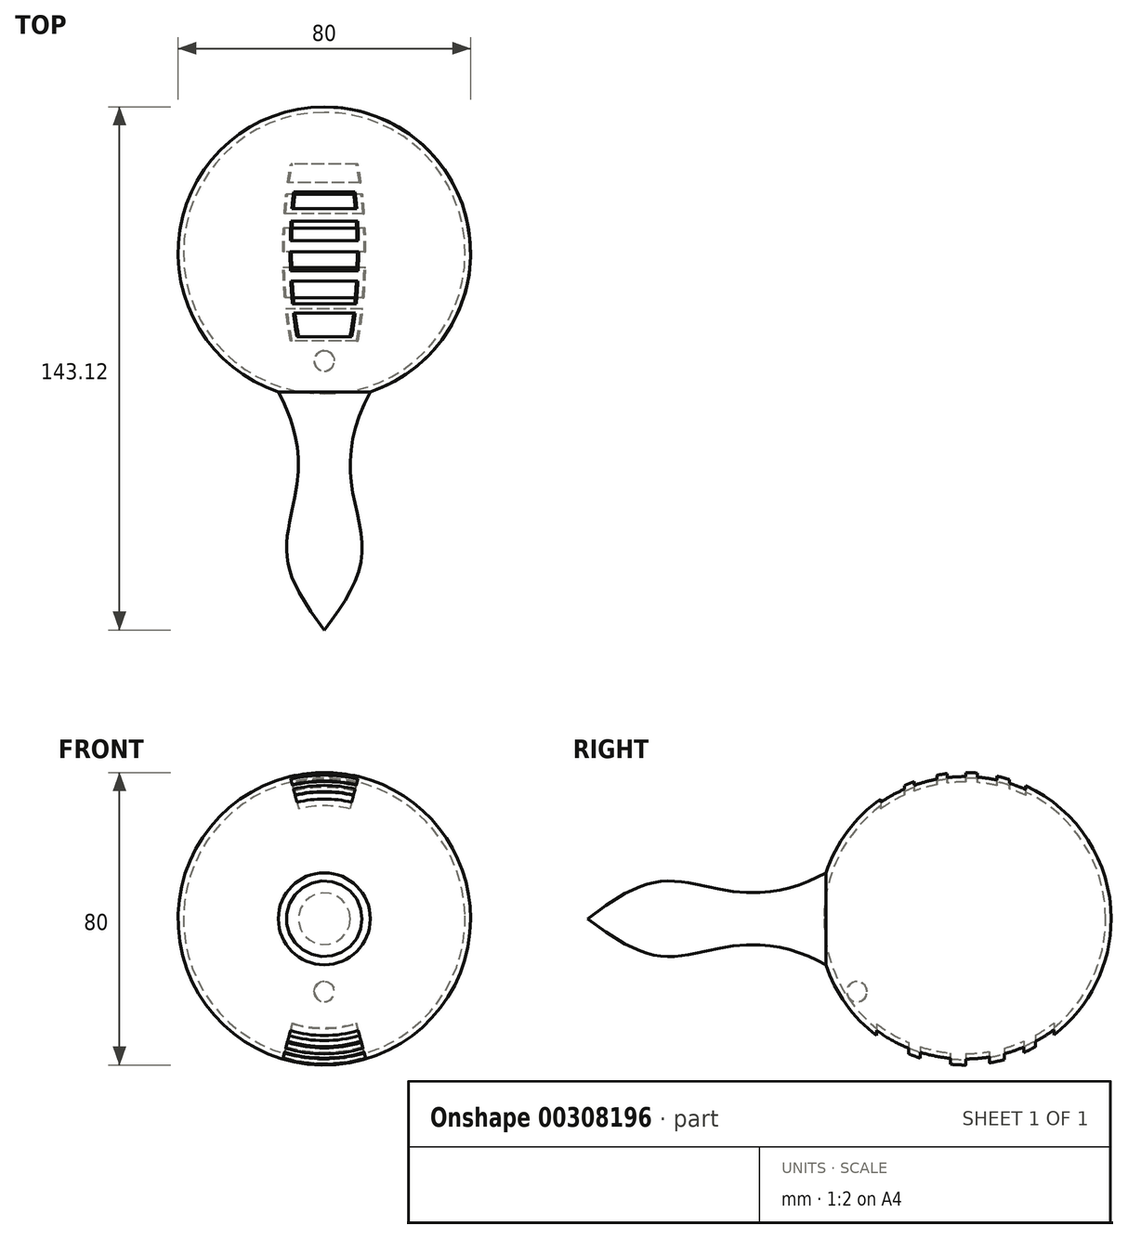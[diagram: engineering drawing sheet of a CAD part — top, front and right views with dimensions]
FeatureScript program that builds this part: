
annotation { "Feature Type Name" : "Feature", "Feature Type Description" : "" }
export const myFeature = defineFeature(function(context is Context, id is Id, definition is map)
    precondition{}
    {
        {
            var Q0;
            Q0=qCreatedBy(makeId("Top.planeOp"),FACE);
            var sketch = newSketch(context, id + "F0", { "sketchPlane" : qUnion([Q0])});
            skArc(sketch, "E0", {"start": v(0, -3.6) * mm, "mid": v(40, 36.4) * mm, "end": v(0, 76.4) * mm});
            skArc(sketch, "E1", {"start": v(0, -2.1) * mm, "mid": v(38.5, 36.4) * mm, "end": v(0, 74.9) * mm});
            skLineSegment(sketch, "E2", {"start": v(0, 76.4) * mm, "end": v(0, -3.6) * mm, "construction": true});
            skLineSegment(sketch, "E3", {"start": v(0, 76.4) * mm, "end": v(0, 74.9) * mm});
            skLineSegment(sketch, "E4", {"start": v(0, -3.6) * mm, "end": v(0, -2.1) * mm});
            skLineSegment(sketch, "E5", {"start": v(12.57, -1.57) * mm, "end": v(12.57, -66.72) * mm, "construction": true});
            skLineSegment(sketch, "E6", {"start": v(12.57, -66.72) * mm, "end": v(0, -66.72) * mm, "construction": true});
            skLineSegment(sketch, "E7", {"start": v(0, -66.72) * mm, "end": v(0, -3.6) * mm, "construction": true});
            skFitSpline(sketch, "E8", {"points": [v(12.57, -1.57) * mm, v(7.43, -26.75) * mm, v(10.25, -46.34) * mm, v(0, -66.72) * mm], "startDerivative": vector(-42.55, -78.05) * mm, "endDerivative": vector(-48.97, -63.58) * mm});
            skLineSegment(sketch, "E9", {"start": v(0, -3.6) * mm, "end": v(0, -66.72) * mm});
            skSolve(sketch);
        }
        {
            var Q0;
            {var subQ2=sQuery(id+"F0.wireOp",EDGE,"E8");Q0=makeQuery(id+"F0.imprint","IMPRINT",FACE,{"disambiguationData":[TD([[makeQuery(id+"F0.imprint","IMPRINT",EDGE,{"derivedFrom":subQ2}),-1.0]])]});}
            var Q1;
            Q1=makeQuery(id+"F0.imprint","IMPRINT",FACE,{"disambiguationData":[TD([[makeQuery(id+"F0.imprint","IMPRINT",EDGE,{"derivedFrom":sQuery(id+"F0.wireOp",EDGE,"E1")}),-1.0]])]});
            var Q2;
            Q2=sQuery(id+"F0.wireOp",EDGE,"E9");
            revolve(context, id + "F1", {"entities" : qUnion([Q0, Q1]), "axis" : qUnion([Q2]), "revolveType" : RevolveType.FULL});
        }
        {
            var Q0;
            Q0=qCreatedBy(makeId("Right.planeOp"),FACE);
            var sketch = newSketch(context, id + "F2", { "sketchPlane" : qUnion([Q0])});
            skLineSegment(sketch, "E10.bottom", {"start": v(13.45, 41.36) * mm, "end": v(19.96, 41.36) * mm});
            skLineSegment(sketch, "E10.top", {"start": v(13.45, 6.23) * mm, "end": v(19.96, 6.23) * mm});
            skLineSegment(sketch, "E10.left", {"start": v(13.45, 41.36) * mm, "end": v(13.45, 6.23) * mm});
            skLineSegment(sketch, "E10.right", {"start": v(19.96, 41.36) * mm, "end": v(19.96, 6.23) * mm});
            skLineSegment(sketch, "E11.bottom", {"start": v(28.74, 41.36) * mm, "end": v(22.51, 41.36) * mm});
            skLineSegment(sketch, "E11.top", {"start": v(28.74, 5.38) * mm, "end": v(22.51, 5.38) * mm});
            skLineSegment(sketch, "E11.left", {"start": v(28.74, 41.36) * mm, "end": v(28.74, 5.38) * mm});
            skLineSegment(sketch, "E11.right", {"start": v(22.51, 41.36) * mm, "end": v(22.51, 5.38) * mm});
            skLineSegment(sketch, "E12.bottom", {"start": v(31.58, 41.64) * mm, "end": v(36.67, 41.64) * mm});
            skLineSegment(sketch, "E12.top", {"start": v(31.58, 3.97) * mm, "end": v(36.67, 3.97) * mm});
            skLineSegment(sketch, "E12.left", {"start": v(31.58, 41.64) * mm, "end": v(31.58, 3.97) * mm});
            skLineSegment(sketch, "E12.right", {"start": v(36.67, 41.64) * mm, "end": v(36.67, 3.97) * mm});
            skLineSegment(sketch, "E13.bottom", {"start": v(39.8, 41.64) * mm, "end": v(45.17, 41.64) * mm});
            skLineSegment(sketch, "E13.top", {"start": v(39.8, 4.25) * mm, "end": v(45.17, 4.25) * mm});
            skLineSegment(sketch, "E13.left", {"start": v(39.8, 41.64) * mm, "end": v(39.8, 4.25) * mm});
            skLineSegment(sketch, "E13.right", {"start": v(45.17, 41.64) * mm, "end": v(45.17, 4.25) * mm});
            skLineSegment(sketch, "E14.bottom", {"start": v(48.57, 41.64) * mm, "end": v(53.1, 41.64) * mm});
            skLineSegment(sketch, "E14.top", {"start": v(48.57, 3.97) * mm, "end": v(53.1, 3.97) * mm});
            skLineSegment(sketch, "E14.left", {"start": v(48.57, 41.64) * mm, "end": v(48.57, 3.97) * mm});
            skLineSegment(sketch, "E14.right", {"start": v(53.1, 41.64) * mm, "end": v(53.1, 3.97) * mm});
            skLineSegment(sketch, "E15.bottom", {"start": v(12.31, -15.01) * mm, "end": v(21.1, -15.01) * mm});
            skLineSegment(sketch, "E15.top", {"start": v(12.31, -49) * mm, "end": v(21.1, -49) * mm});
            skLineSegment(sketch, "E15.left", {"start": v(12.31, -15.01) * mm, "end": v(12.31, -49) * mm});
            skLineSegment(sketch, "E15.right", {"start": v(21.1, -15.01) * mm, "end": v(21.1, -49) * mm});
            skLineSegment(sketch, "E16.bottom", {"start": v(24.21, -15.3) * mm, "end": v(32.43, -15.3) * mm});
            skLineSegment(sketch, "E16.top", {"start": v(24.21, -48.44) * mm, "end": v(32.43, -48.44) * mm});
            skLineSegment(sketch, "E16.left", {"start": v(24.21, -15.3) * mm, "end": v(24.21, -48.44) * mm});
            skLineSegment(sketch, "E16.right", {"start": v(32.43, -15.3) * mm, "end": v(32.43, -48.44) * mm});
            skLineSegment(sketch, "E17.bottom", {"start": v(36.67, -15.58) * mm, "end": v(43.19, -15.58) * mm});
            skLineSegment(sketch, "E17.top", {"start": v(36.67, -49) * mm, "end": v(43.19, -49) * mm});
            skLineSegment(sketch, "E17.left", {"start": v(36.67, -15.58) * mm, "end": v(36.67, -49) * mm});
            skLineSegment(sketch, "E17.right", {"start": v(43.19, -15.58) * mm, "end": v(43.19, -49) * mm});
            skLineSegment(sketch, "E18.bottom", {"start": v(47.16, -15.01) * mm, "end": v(52.54, -15.01) * mm});
            skLineSegment(sketch, "E18.top", {"start": v(47.16, -49.29) * mm, "end": v(52.54, -49.29) * mm});
            skLineSegment(sketch, "E18.left", {"start": v(47.16, -15.01) * mm, "end": v(47.16, -49.29) * mm});
            skLineSegment(sketch, "E18.right", {"start": v(52.54, -15.01) * mm, "end": v(52.54, -49.29) * mm});
            skLineSegment(sketch, "E19.bottom", {"start": v(55.65, -15.58) * mm, "end": v(60.75, -15.58) * mm});
            skLineSegment(sketch, "E19.top", {"start": v(55.65, -49) * mm, "end": v(60.75, -49) * mm});
            skLineSegment(sketch, "E19.left", {"start": v(55.65, -15.58) * mm, "end": v(55.65, -49) * mm});
            skLineSegment(sketch, "E19.right", {"start": v(60.75, -15.58) * mm, "end": v(60.75, -49) * mm});
            skLineSegment(sketch, "E20.bottom", {"start": v(13.45, 35.4) * mm, "end": v(53.1, 35.4) * mm, "construction": true});
            skLineSegment(sketch, "E20.top", {"start": v(12.31, -41.36) * mm, "end": v(60.75, -41.36) * mm, "construction": true});
            skSolve(sketch);
        }
        {
            var Q0;
            Q0 = qSketchRegion(id + "F2", true);
            var Q1;
            Q1=sQuery(id+"F2.wireOp",EDGE,"E14.top");
            revolve(context, id + "F3", {"operationType" : NewBodyOperationType.REMOVE, "entities" : qUnion([Q0]), "axis" : qUnion([Q1]), "revolveType" : RevolveType.SYMMETRIC, "oppositeDirection" : true, "angle" : 30 * degree});
        }
        {
            var Q0;
            Q0=qCreatedBy(makeId("Right.planeOp"),FACE);
            var sketch = newSketch(context, id + "F4", { "sketchPlane" : qUnion([Q0])});
            skArc(sketch, "E21", {"start": v(6.84, -17.17) * mm, "mid": v(4.18, -19.99) * mm, "end": v(6.94, -22.7) * mm});
            skLineSegment(sketch, "E22", {"start": v(6.84, -17.17) * mm, "end": v(6.94, -22.7) * mm, "construction": true});
            skLineSegment(sketch, "E23", {"start": v(6.84, -17.17) * mm, "end": v(6.94, -22.7) * mm});
            skSolve(sketch);
        }
        {
            var Q0;
            Q0 = qSketchRegion(id + "F4", true);
            var Q1;
            Q1=sQuery(id+"F4.wireOp",EDGE,"E23");
            revolve(context, id + "F5", {"entities" : qUnion([Q0]), "axis" : qUnion([Q1]), "revolveType" : RevolveType.FULL});
        }
    });
